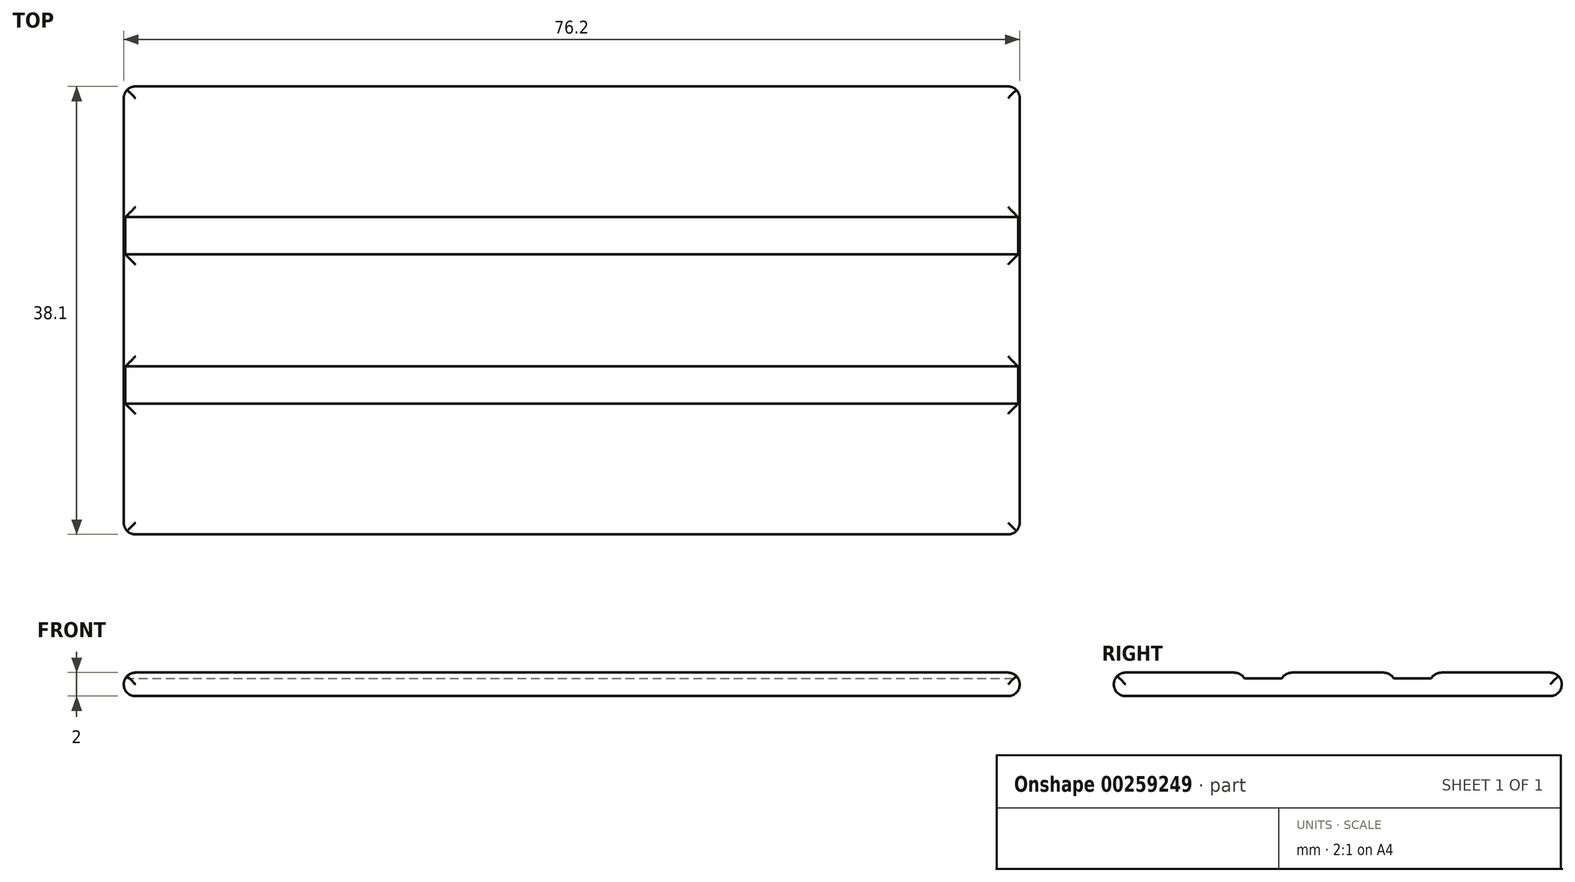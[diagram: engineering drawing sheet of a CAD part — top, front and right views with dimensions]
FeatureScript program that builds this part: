
annotation { "Feature Type Name" : "Feature", "Feature Type Description" : "" }
export const myFeature = defineFeature(function(context is Context, id is Id, definition is map)
    precondition{}
    {
        {
            var Q0;
            Q0=qCreatedBy(makeId("Top.planeOp"),FACE);
            var sketch = newSketch(context, id + "F0", { "sketchPlane" : qUnion([Q0])});
            skLineSegment(sketch, "E0.bottom", {"start": v(-27.1, 4.97) * mm, "end": v(49.1, 4.97) * mm});
            skLineSegment(sketch, "E0.top", {"start": v(-27.1, -33.13) * mm, "end": v(49.1, -33.13) * mm});
            skLineSegment(sketch, "E0.left", {"start": v(-27.1, 4.97) * mm, "end": v(-27.1, -33.13) * mm});
            skLineSegment(sketch, "E0.right", {"start": v(49.1, 4.97) * mm, "end": v(49.1, -33.13) * mm});
            skPoint(sketch, "E1", {"position": v(-27.1, -20.43) * mm});
            skPoint(sketch, "E2", {"position": v(-27.1, -7.73) * mm});
            skPoint(sketch, "E3", {"position": v(-27.1, -9.31) * mm});
            skPoint(sketch, "E4", {"position": v(-27.1, -6.14) * mm});
            skPoint(sketch, "E5", {"position": v(-27.1, -18.84) * mm});
            skPoint(sketch, "E6", {"position": v(-27.1, -22.01) * mm});
            skLineSegment(sketch, "E7", {"start": v(-27.1, -6.14) * mm, "end": v(49.1, -6.14) * mm});
            skLineSegment(sketch, "E8", {"start": v(-27.1, -9.31) * mm, "end": v(49.1, -9.31) * mm});
            skLineSegment(sketch, "E9", {"start": v(-27.1, -18.84) * mm, "end": v(49.1, -18.84) * mm});
            skLineSegment(sketch, "E10", {"start": v(-27.1, -22.01) * mm, "end": v(49.1, -22.01) * mm});
            skSolve(sketch);
        }
        {
            var Q0;
            {var subQ0=sQuery(id+"F0.wireOp",EDGE,"E0.bottom");Q0=makeQuery(id+"F0.imprint","IMPRINT",FACE,{"disambiguationData":[TD([[makeQuery(id+"F0.imprint","IMPRINT",EDGE,{"derivedFrom":subQ0}),-1.0]])]});}
            var Q1;
            {var subQ0=sQuery(id+"F0.wireOp",EDGE,"E8");Q1=makeQuery(id+"F0.imprint","IMPRINT",FACE,{"disambiguationData":[TD([[makeQuery(id+"F0.imprint","IMPRINT",EDGE,{"derivedFrom":subQ0}),-1.0]])]});}
            var Q2;
            {var subQ0=sQuery(id+"F0.wireOp",EDGE,"E0.top");Q2=makeQuery(id+"F0.imprint","IMPRINT",FACE,{"disambiguationData":[TD([[makeQuery(id+"F0.imprint","IMPRINT",EDGE,{"derivedFrom":subQ0}),1.0]])]});}
            extrude(context, id + "F1", {"entities" : qUnion([Q0, Q1, Q2]), "depth" : 2 * mm, "offsetDistance" : 25.4 * mm});
        }
        {
            var Q0;
            {var subQ0=sQuery(id+"F0.wireOp",EDGE,"E7");Q0=makeQuery(id+"F0.imprint","IMPRINT",FACE,{"disambiguationData":[TD([[makeQuery(id+"F0.imprint","IMPRINT",EDGE,{"derivedFrom":subQ0}),-1.0]])]});}
            var Q1;
            {var subQ0=sQuery(id+"F0.wireOp",EDGE,"E9");Q1=makeQuery(id+"F0.imprint","IMPRINT",FACE,{"disambiguationData":[TD([[makeQuery(id+"F0.imprint","IMPRINT",EDGE,{"derivedFrom":subQ0}),-1.0]])]});}
            extrude(context, id + "F2", {"entities" : qUnion([Q0, Q1]), "operationType" : NewBodyOperationType.ADD, "depth" : 1.5 * mm, "offsetDistance" : 25.4 * mm});
        }
        {
            var Q0;
            Q0=makeQuery(id+"F1.opExtrude","SWEPT_FACE",FACE,{"disambiguationData":[OSD([sQuery(id+"F0.wireOp",EDGE,"E0.top")])]});
            var Q1;
            Q1=makeQuery(id+"F1.opExtrude","SWEPT_FACE",FACE,{"disambiguationData":[OSD([sQuery(id+"F0.wireOp",EDGE,"E0.bottom")])]});
            var Q2;
            Q2=makeQuery(id+"F1.opExtrude","CAP_FACE",FACE,{"disambiguationData":[OSD([sQuery(id+"F0.wireOp",EDGE,"E0.left"),sQuery(id+"F0.wireOp",EDGE,"E0.right"),sQuery(id+"F0.wireOp",EDGE,"E8"),sQuery(id+"F0.wireOp",EDGE,"E9")])],"isStart":false});
            fillet(context, id + "F3", {"entities" : qUnion([Q0, Q1, Q2]), "radius" : 1 * mm, "tangentPropagation" : true, "allowEdgeOverflow" : false});
        }
        {
            var Q0;
            {var subQ0=sQuery(id+"F0.wireOp",EDGE,"E0.right");var subQ1=makeQuery(id+"F0.imprint","INTERSECT",VERTEX,{"derivedFrom":[subQ0,sQuery(id+"F0.wireOp",EDGE,"E9")]});var subQ3=makeQuery(id+"F0.imprint","INTERSECT",VERTEX,{"derivedFrom":[subQ0,sQuery(id+"F0.wireOp",EDGE,"E7")]});var subQ4=makeQuery(id+"F0.imprint","INTERSECT",VERTEX,{"derivedFrom":[subQ0,sQuery(id+"F0.wireOp",EDGE,"E8")]});Q0=makeQuery(id+"F2.boolean.opBoolean","MERGE",EDGE,{"derivedFrom":[makeQuery(id+"F1.opExtrude","CAP_EDGE",EDGE,{"disambiguationData":[OSD([subQ0]),TDD([makeQuery(id+"F0.imprint","IMPRINT",EDGE,{"disambiguationData":[TD([[makeQuery(id+"F0.imprint","INTERSECT",VERTEX,{"derivedFrom":[sQuery(id+"F0.wireOp",EDGE,"E0.bottom"),subQ0]}),-1.0]])],"derivedFrom":subQ0})])],"isStart":true}),makeQuery(id+"F1.opExtrude","CAP_EDGE",EDGE,{"disambiguationData":[OSD([subQ0]),TDD([makeQuery(id+"F0.imprint","IMPRINT",EDGE,{"disambiguationData":[TD([[subQ4,-1.0]])],"derivedFrom":subQ0})])],"isStart":true}),makeQuery(id+"F1.opExtrude","CAP_EDGE",EDGE,{"disambiguationData":[OSD([subQ0]),TDD([makeQuery(id+"F0.imprint","IMPRINT",EDGE,{"disambiguationData":[TD([[makeQuery(id+"F0.imprint","INTERSECT",VERTEX,{"derivedFrom":[sQuery(id+"F0.wireOp",EDGE,"E0.top"),subQ0]}),1.0]])],"derivedFrom":subQ0})])],"isStart":true}),makeQuery(id+"F2.opExtrude","CAP_EDGE",EDGE,{"disambiguationData":[OSD([subQ0]),TDD([makeQuery(id+"F0.imprint","IMPRINT",EDGE,{"disambiguationData":[TD([[subQ3,-1.0]])],"derivedFrom":subQ0})])],"isStart":true}),makeQuery(id+"F2.opExtrude","CAP_EDGE",EDGE,{"disambiguationData":[OSD([subQ0]),TDD([makeQuery(id+"F0.imprint","IMPRINT",EDGE,{"disambiguationData":[TD([[subQ1,-1.0]])],"derivedFrom":subQ0})])],"isStart":true})]});}
            var Q1;
            {var subQ0=sQuery(id+"F0.wireOp",EDGE,"E0.left");var subQ1=makeQuery(id+"F0.imprint","INTERSECT",VERTEX,{"derivedFrom":[subQ0,sQuery(id+"F0.wireOp",EDGE,"E9")]});var subQ3=makeQuery(id+"F0.imprint","INTERSECT",VERTEX,{"derivedFrom":[subQ0,sQuery(id+"F0.wireOp",EDGE,"E7")]});var subQ4=makeQuery(id+"F0.imprint","INTERSECT",VERTEX,{"derivedFrom":[subQ0,sQuery(id+"F0.wireOp",EDGE,"E8")]});Q1=makeQuery(id+"F2.boolean.opBoolean","MERGE",EDGE,{"derivedFrom":[makeQuery(id+"F1.opExtrude","CAP_EDGE",EDGE,{"disambiguationData":[OSD([subQ0]),TDD([makeQuery(id+"F0.imprint","IMPRINT",EDGE,{"disambiguationData":[TD([[makeQuery(id+"F0.imprint","INTERSECT",VERTEX,{"derivedFrom":[sQuery(id+"F0.wireOp",EDGE,"E0.bottom"),subQ0]}),-1.0]])],"derivedFrom":subQ0})])],"isStart":true}),makeQuery(id+"F1.opExtrude","CAP_EDGE",EDGE,{"disambiguationData":[OSD([subQ0]),TDD([makeQuery(id+"F0.imprint","IMPRINT",EDGE,{"disambiguationData":[TD([[subQ4,-1.0]])],"derivedFrom":subQ0})])],"isStart":true}),makeQuery(id+"F1.opExtrude","CAP_EDGE",EDGE,{"disambiguationData":[OSD([subQ0]),TDD([makeQuery(id+"F0.imprint","IMPRINT",EDGE,{"disambiguationData":[TD([[makeQuery(id+"F0.imprint","INTERSECT",VERTEX,{"derivedFrom":[sQuery(id+"F0.wireOp",EDGE,"E0.top"),subQ0]}),1.0]])],"derivedFrom":subQ0})])],"isStart":true}),makeQuery(id+"F2.opExtrude","CAP_EDGE",EDGE,{"disambiguationData":[OSD([subQ0]),TDD([makeQuery(id+"F0.imprint","IMPRINT",EDGE,{"disambiguationData":[TD([[subQ3,-1.0]])],"derivedFrom":subQ0})])],"isStart":true}),makeQuery(id+"F2.opExtrude","CAP_EDGE",EDGE,{"disambiguationData":[OSD([subQ0]),TDD([makeQuery(id+"F0.imprint","IMPRINT",EDGE,{"disambiguationData":[TD([[subQ1,-1.0]])],"derivedFrom":subQ0})])],"isStart":true})]});}
            var Q2;
            Q2=makeQuery(id+"F1.opExtrude","CAP_EDGE",EDGE,{"disambiguationData":[OSD([sQuery(id+"F0.wireOp",EDGE,"E10")])],"isStart":false});
            var Q3;
            Q3=makeQuery(id+"F1.opExtrude","CAP_EDGE",EDGE,{"disambiguationData":[OSD([sQuery(id+"F0.wireOp",EDGE,"E7")])],"isStart":false});
            fillet(context, id + "F4", {"entities" : qUnion([Q0, Q1, Q2, Q3]), "radius" : 1 * mm, "tangentPropagation" : true, "allowEdgeOverflow" : false});
        }
    });
